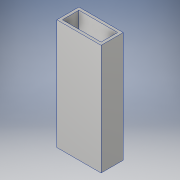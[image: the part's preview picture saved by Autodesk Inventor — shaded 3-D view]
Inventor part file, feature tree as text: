
AUTODESK INVENTOR PART (.ipt)
format: ipt  version: 2018 (Build 220112000, 112)  size: 100,864 bytes
history: native  units: in
note: dims shown in document units (in); Inventor stores cm internally (conversion verified against a paired STEP export)
features: extrude x1, sketch x1
ambient origin geometry x8: Origin, YZ Plane, XZ Plane, XY Plane, X Axis, Y Axis, Z Axis, Center Point
bodies: Solid1 (feature_tree)
feature tree (2):
  extrude  "Extrusion1"  Depth=1.0in
  sketch  "Sketch1"  dims[d0=2.0in d1=1.0in d2=0.125in d3=0.125in d4=0.125in d5=0.125in d6=5.0in d7=0.0in]
